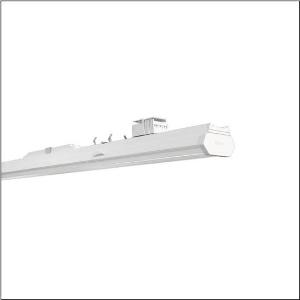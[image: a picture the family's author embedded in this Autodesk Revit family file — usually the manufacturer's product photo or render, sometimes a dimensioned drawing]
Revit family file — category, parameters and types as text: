
# Revit family: licross_r__21_protected_ho_52tp11dn4dxs_9872
name_source: partatom
category: Lighting Fixtures
units: mm (PartAtom-declared; Revit-internal decimal feet)

## family parameters
Cut with Voids When Loaded = No
Host = Face
Light Source = No
Part Type = Normal
Room Calculation Point = No
Round Connector Dimension = Use Diameter
Shared = No

## types (1)
- --- (1 x LED, 13000 lm, 73.1 W, 4000K)
    Apparent Load = 73 VA
    CIE Flux Codes = 84 94 98 99 100
    Color Rendering = 80
    Color Temperature = 4000K
    Default Elevation = 1800 mm
    Description = Licross® 21 Protected HO, luminaire insert, of sheet steel, galvanised, coil coated, white, length: 1.500mm, width: 90mm, height: 103mm, LED rated luminous flux: 13.000lm, light colour: 840, SDCM (Standard Deviation of Colour Matching)MacAdam ≤ 3 SDCM (initial), control gear: DALI 2, with plug, 5-pole, with phase selection, mains connection: 220..240V, AC, 50/60Hz, rated input power: 73W, internal wiring halogen-free, primary light control with lens, of plastic, primary optical cover: cover, of PMMA, light emission: direct distribution, primary light characteristic: symmetric, protection rating (complete): IP64, insulation class (complete): insulation class I (protective earthing), certification: CE, ENEC, VDE, UKCA, protection symbol: D if used in an environment with conductive dust loads with corresponding accessories, impact resistance: IK06, permissible ambient temperature for indoor applications: -25..+40°C, corresponds to IFS (International Featured Standards) requirements for safety and quality in the food industry, reducing of maximum allowable ambient temperature of 5°C with ceiling mounting, LABS conformity tested according to VDMA 24364:2018-05, packaging unit: 1 piece
    Height = 92 mm
    Lamp = 1 x LED
    Lamp Light Flux = 13000 lm
    Lamp Power = 73.1 W
    Lamp count = 1
    Length = 1500 mm
    Luminous efficacy = 178 lm/W
    Manufacturer = Siteco
    ModVariant = No
    Model = 52TP11DN4DXS
    Mounting Place = Ceiling
    Mounting Type = Pendant
    Number of Poles = 1
    OnlyDefault = Yes
    Power Factor = 1
    Product Name = Licross® 21 Protected HO
    Product group = luminaire insert | ceiling pendant
    ProductGroupID = 901
    Protection Class = Protection class I
    Protection Degree = IP 64
    RLX_Detail_Level = 1
    RLX_Emergency_Light_Flux = 0 lm
    RLX_Emergency_Type = 0
    RLX_Emergency_Type_DB = No
    RlxData = <blob elided: 24429 chars, md5=b8c67213>
    Socket = socket
    Standby Power = 0 W
    System Light Flux = 13000 lm
    System Power = 73 W
    Type Comments = factory setting: luminous flux: 100 % | dim-lin: 254 | 417 mA
    Type Image = l_1256148.jpg
    URL = http://relux.com
    VarID = @adj_132291
    Voltage = 0 V
    Weight = 0.00 kg
    Width = 88 mm

## geometry (parser evidence)
native form markers: Blend x4, Sweep x10
no freeform markers — native parametric forms only
